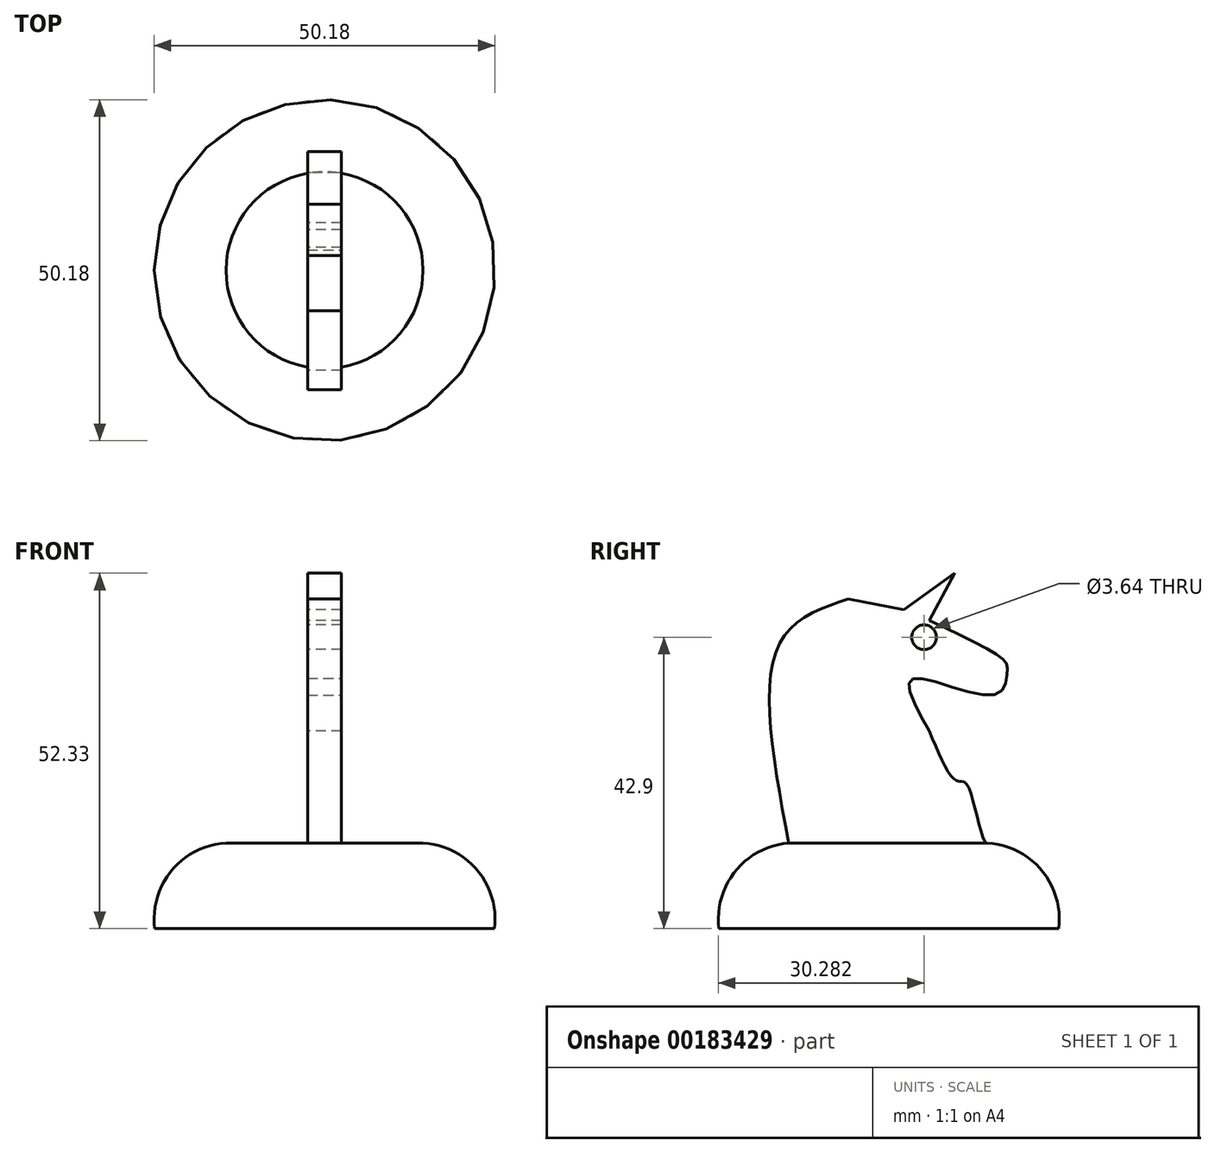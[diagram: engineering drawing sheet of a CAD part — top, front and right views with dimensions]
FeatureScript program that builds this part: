
annotation { "Feature Type Name" : "Feature", "Feature Type Description" : "" }
export const myFeature = defineFeature(function(context is Context, id is Id, definition is map)
    precondition{}
    {
        {
            var Q0;
            Q0=qCreatedBy(makeId("Front.planeOp"),FACE);
            var sketch = newSketch(context, id + "F0", { "sketchPlane" : qUnion([Q0])});
            skLineSegment(sketch, "E0", {"start": v(0, 0) * mm, "end": v(25, 0) * mm});
            skLineSegment(sketch, "E1.MirrorCS", {"start": v(0, 0) * mm, "end": v(-25, 0) * mm});
            skLineSegment(sketch, "E2", {"start": v(0, 0) * mm, "end": v(0, 12.81) * mm});
            skArc(sketch, "E3", {"start": v(25, 0) * mm, "mid": v(22.5, 8.6) * mm, "end": v(14.5, 12.61) * mm});
            skArc(sketch, "E4.MirrorCS", {"start": v(-25, 0) * mm, "mid": v(-22.5, 8.6) * mm, "end": v(-14.5, 12.61) * mm});
            skLineSegment(sketch, "E5", {"start": v(14.5, 12.61) * mm, "end": v(-14.5, 12.61) * mm});
            skSolve(sketch);
        }
        {
            var Q0;
            Q0=makeQuery(id+"F0.imprint","IMPRINT",FACE,{"disambiguationData":[TD([[makeQuery(id+"F0.imprint","IMPRINT",EDGE,{"derivedFrom":sQuery(id+"F0.wireOp",EDGE,"E0")}),1.0]])]});
            var Q1;
            Q1=sQuery(id+"F0.wireOp",EDGE,"E2");
            revolve(context, id + "F1", {"entities" : qUnion([Q0]), "axis" : qUnion([Q1]), "revolveType" : RevolveType.FULL});
        }
        {
            var Q0;
            Q0=qCreatedBy(makeId("Right.planeOp"),FACE);
            var sketch = newSketch(context, id + "F2", { "sketchPlane" : qUnion([Q0])});
            skLineSegment(sketch, "E6", {"start": v(-5.96, 48.56) * mm, "end": v(2.18, 46.97) * mm});
            skLineSegment(sketch, "E7", {"start": v(2.18, 46.97) * mm, "end": v(9.73, 52.33) * mm});
            skLineSegment(sketch, "E8", {"start": v(9.73, 52.33) * mm, "end": v(5.96, 45.38) * mm});
            skFitSpline(sketch, "E9", {"points": [v(5.96, 45.38) * mm, v(16.94, 39.54) * mm, v(17.43, 37.95) * mm, v(15.75, 34.48) * mm, v(3.53, 36.76) * mm, v(5.96, 29.12) * mm], "startDerivative": vector(53.9, -25.1) * mm, "endDerivative": vector(27.79, -49.15) * mm});
            skFitSpline(sketch, "E10", {"points": [v(5.96, 29.12) * mm, v(9.99, 21.77) * mm, v(11.38, 21.37) * mm, v(14.16, 12.83) * mm, v(14.55, 12.51) * mm, v(14.36, 12.51) * mm], "startDerivative": vector(12.09, -29.29) * mm, "endDerivative": vector(-5.27, 0.1) * mm});
            skLineSegment(sketch, "E11", {"start": v(14.55, 12.51) * mm, "end": v(-14.73, 12.51) * mm});
            skFitSpline(sketch, "E12", {"points": [v(-5.96, 48.56) * mm, v(-16.09, 42) * mm, v(-14.73, 12.51) * mm], "startDerivative": vector(-31.47, -10.66) * mm, "endDerivative": vector(10.82, -57.97) * mm});
            skSolve(sketch);
        }
        {
            var Q0;
            Q0=makeQuery(id+"F2.imprint","IMPRINT",FACE,{"disambiguationData":[TD([[makeQuery(id+"F2.imprint","IMPRINT",EDGE,{"derivedFrom":sQuery(id+"F2.wireOp",EDGE,"E6")}),-1.0]])]});
            extrude(context, id + "F3", {"entities" : qUnion([Q0]), "operationType" : NewBodyOperationType.ADD, "endBound" : BoundingType.SYMMETRIC, "depth" : 5 * mm});
        }
        {
            var Q0;
            Q0=makeQuery(id+"F3.opExtrude","CAP_FACE",FACE,{"disambiguationData":[OSD([sQuery(id+"F2.wireOp",EDGE,"ewwOclgY-0H0G-XBYP-dfVQ-jouC9pT5QdZx"),sQuery(id+"F2.wireOp",EDGE,"CZKMW3KF-eYRq-MXls-DdER-TS31ygk0F0WE"),sQuery(id+"F2.wireOp",EDGE,"RoTj8U1b-WUJB-KEsy-jwFo-amj9rYAu6Huc"),sQuery(id+"F2.wireOp",EDGE,"ECO86PAB-YGui-PldG-5hRX-W9z8cKTmAZ5L"),sQuery(id+"F2.wireOp",EDGE,"EO5HI7gf-4eBT-BLIy-mCkU-7LWnqwp0452t"),sQuery(id+"F2.wireOp",EDGE,"E6"),sQuery(id+"F2.wireOp",EDGE,"E7"),sQuery(id+"F2.wireOp",EDGE,"E8"),sQuery(id+"F2.wireOp",EDGE,"E9"),sQuery(id+"F2.wireOp",EDGE,"E10"),sQuery(id+"F2.wireOp",EDGE,"E11")])],"isStart":true});
            var sketch = newSketch(context, id + "F4", { "sketchPlane" : qUnion([Q0])});
            skCircle(sketch, "E13", {"center": v(-5.2, 42.9) * mm, "radius": 1.82 * mm});
            skSolve(sketch);
        }
        {
            var Q0;
            Q0=qSketchRegion(id+"F4",true);
            extrude(context, id + "F5", {"entities" : qUnion([Q0]), "operationType" : NewBodyOperationType.REMOVE, "endBound" : BoundingType.SYMMETRIC, "oppositeDirection" : true, "depth" : 25 * mm});
        }
    });
